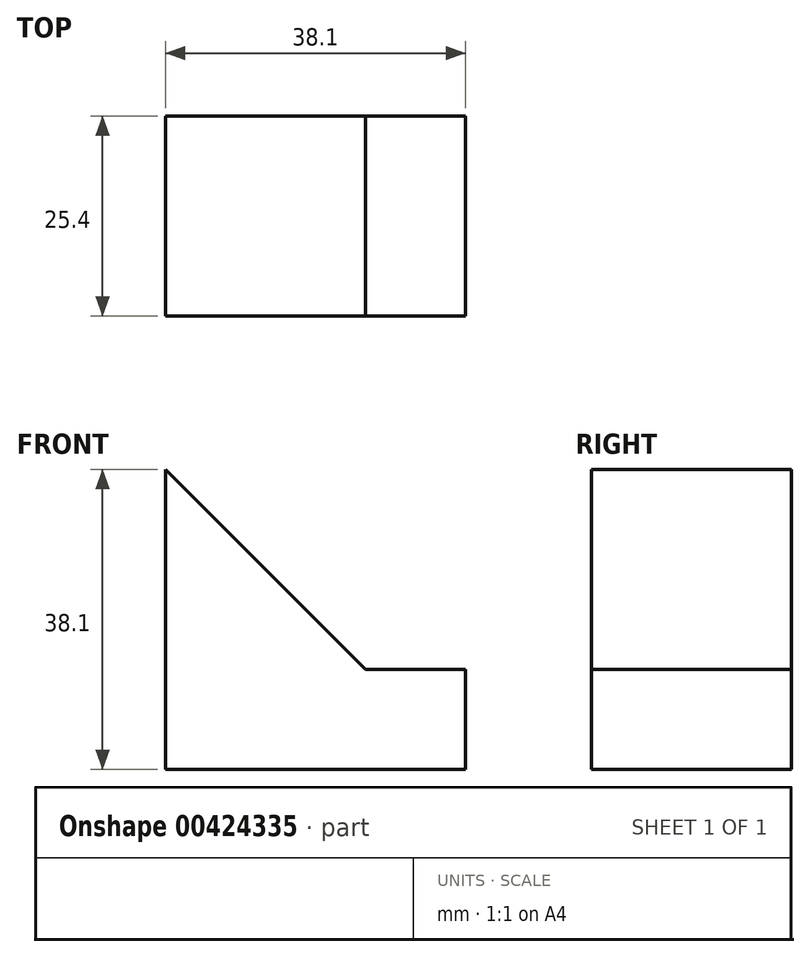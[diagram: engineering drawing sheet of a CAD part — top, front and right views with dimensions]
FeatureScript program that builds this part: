
annotation { "Feature Type Name" : "Feature", "Feature Type Description" : "" }
export const myFeature = defineFeature(function(context is Context, id is Id, definition is map)
    precondition{}
    {
        {
            var Q0;
            Q0=qCreatedBy(makeId("Front.planeOp"),FACE);
            var sketch = newSketch(context, id + "F0", { "sketchPlane" : qUnion([Q0])});
            skLineSegment(sketch, "E0", {"start": v(0, 0) * mm, "end": v(38.1, 0) * mm});
            skLineSegment(sketch, "E1", {"start": v(38.1, 0) * mm, "end": v(38.1, 12.7) * mm});
            skLineSegment(sketch, "E2", {"start": v(38.1, 12.7) * mm, "end": v(25.4, 12.7) * mm});
            skLineSegment(sketch, "E3", {"start": v(0, 0) * mm, "end": v(0, 38.1) * mm});
            skLineSegment(sketch, "E4", {"start": v(0, 38.1) * mm, "end": v(25.4, 12.7) * mm});
            skSolve(sketch);
        }
        {
            var Q0;
            Q0=makeQuery(id+"F0.imprint","IMPRINT",FACE,{"disambiguationData":[TD([[makeQuery(id+"F0.imprint","IMPRINT",EDGE,{"derivedFrom":sQuery(id+"F0.wireOp",EDGE,"E0")}),1.0]])]});
            extrude(context, id + "F1", {"entities" : qUnion([Q0]), "depth" : 25.4 * mm});
        }
    });
